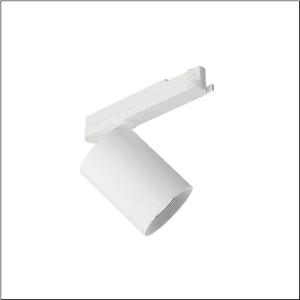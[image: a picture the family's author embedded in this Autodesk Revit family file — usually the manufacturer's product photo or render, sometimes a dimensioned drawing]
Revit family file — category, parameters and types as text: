
# Revit family: spot_21_51se14mbb5b
name_source: partatom
category: Lighting Fixtures
units: mm (PartAtom-declared; Revit-internal decimal feet)

## family parameters
Cut with Voids When Loaded = No
Host = Face
Light Source = No
Part Type = Normal
Room Calculation Point = No
Round Connector Dimension = Use Diameter
Shared = No

## types (1)
- --- (1 x LED, 5530 lm, 41.8 W, 3000K)
    Apparent Load = 42 VA
    CIE Flux Codes = 96 99 100 100 100
    Color Rendering = 90
    Color Temperature = 3000K
    Default Elevation = 1800 mm
    Description = Spot 21, directional spotlight, light control with lens, of PMMA, LED rated luminous flux: 5.110lm, light colour: 930, control gear: ECG Multilumen, with 3-phase adapter, mains connection: 220..240V, AC, 50/60Hz, of aluminium, traffic white (RAL 9016), length: 213mm, diameter: 105mm, protection rating (complete): IP20, insulation class (complete): insulation class I (protective earthing), certification: CE, impact resistance: IK02, permissible ambient temperature for indoor applications: -20..+40°C, packaging unit: 1 piece
    Height = 175 mm
    Lamp = 1 x LED
    Lamp Light Flux = 5530 lm
    Lamp Power = 41.8 W
    Lamp count = 1
    Length = 105 mm
    Luminous efficacy = 132 lm/W
    Manufacturer = Siteco
    ModVariant = No
    Model = 51SE14MBB5B
    Mounting Place = Ceiling
    Mounting Type = Pendant
    Number of Poles = 1
    OnlyDefault = Yes
    Power Factor = 1
    Product Name = Spot 21
    Product group = directional spotlight
    ProductGroupID = 905
    Protection Class = Protection class I
    Protection Degree = IP 20
    RLX_Detail_Level = 1
    RLX_Emergency_Light_Flux = 0 lm
    RLX_Emergency_Type = 0
    RLX_Emergency_Type_DB = No
    RlxData = <blob elided: 17661 chars, md5=27e09c2f>
    Socket = socket
    Standby Power = 0 W
    System Light Flux = 5530 lm
    System Power = 42 W
    Type Comments = factory setting: luminous flux: 100 % | (ON | ON | ON | ON) | 1050 mA
    Type Image = l_1003976.jpg
    URL = http://relux.com
    VarID = @adj_075189
    Voltage = 0 V
    Weight = 0.00 kg
    Width = 0 mm  [stored 0 ft]

note: [stored X ft] marks values corroborated as IEEE doubles in the binary element streams (Revit-internal decimal feet)

## geometry (parser evidence)
native form markers: Blend x4, Sweep x11
no freeform markers — native parametric forms only
